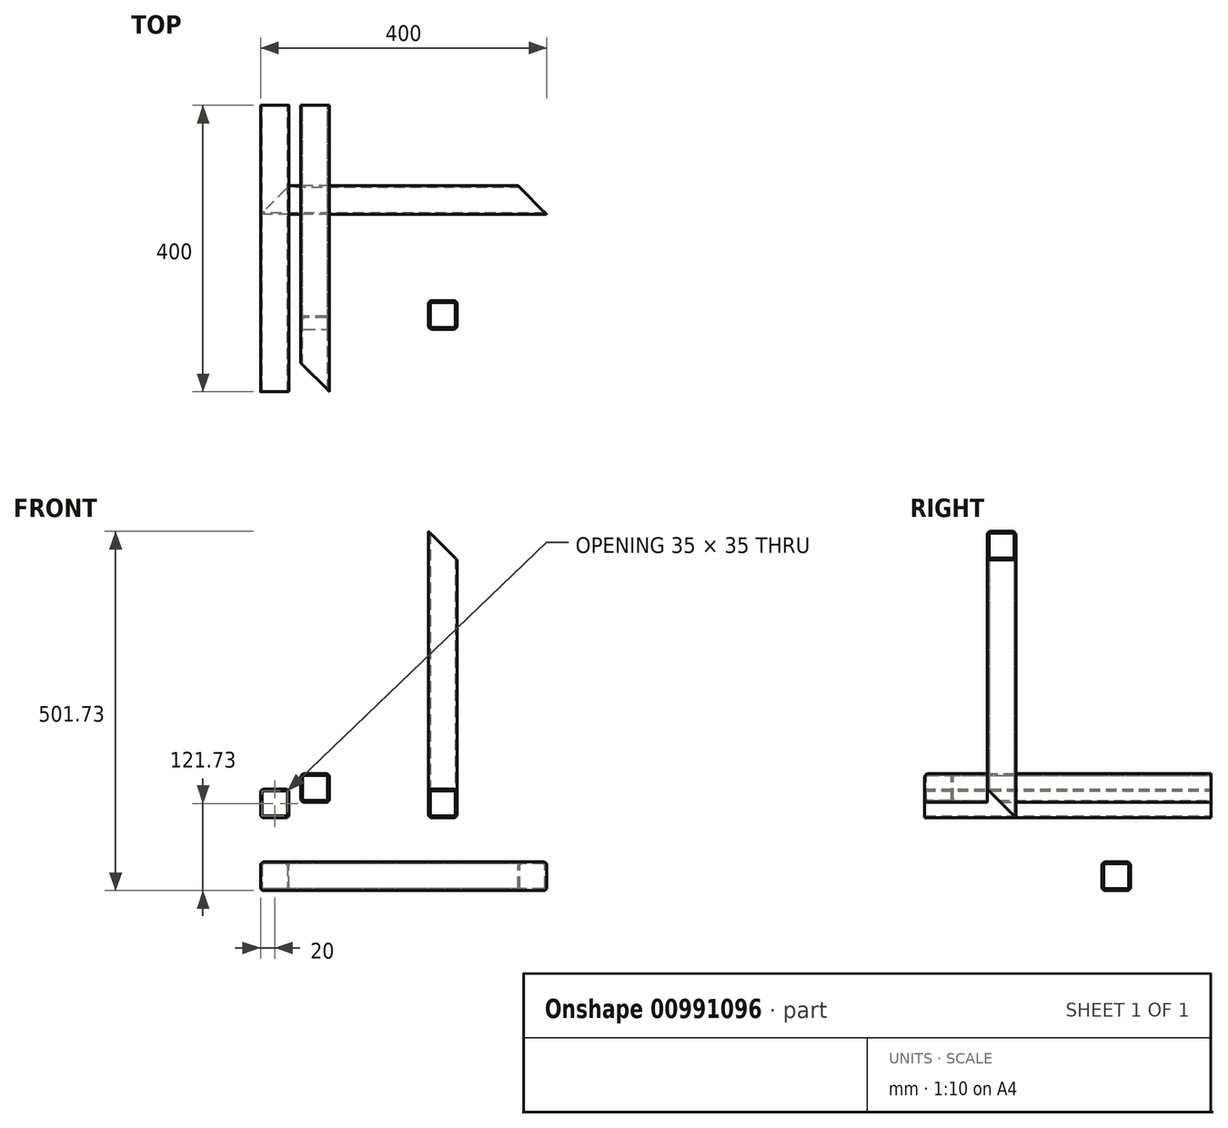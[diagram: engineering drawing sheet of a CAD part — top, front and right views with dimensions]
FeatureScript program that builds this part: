
annotation { "Feature Type Name" : "Feature", "Feature Type Description" : "" }
export const myFeature = defineFeature(function(context is Context, id is Id, definition is map)
    precondition{}
    {
        {
            var Q0;
            Q0=qCreatedBy(makeId("Front.planeOp"),FACE);
            var sketch = newSketch(context, id + "F0", { "sketchPlane" : qUnion([Q0])});
            skLineSegment(sketch, "E0.bottom", {"start": v(5, 0) * mm, "end": v(35, 0) * mm});
            skLineSegment(sketch, "E0.top", {"start": v(5, 40) * mm, "end": v(35, 40) * mm});
            skLineSegment(sketch, "E0.left", {"start": v(0, 5) * mm, "end": v(0, 35) * mm});
            skLineSegment(sketch, "E0.right", {"start": v(40, 5) * mm, "end": v(40, 35) * mm});
            skPoint(sketch, "E1.visualSharp", {"position": v(0, 40) * mm});
            skArc(sketch, "E1.filletArc", {"start": v(5, 40) * mm, "mid": v(1.46, 38.54) * mm, "end": v(0, 35) * mm});
            skPoint(sketch, "E2.visualSharp", {"position": v(40, 40) * mm});
            skArc(sketch, "E2.filletArc", {"start": v(40, 35) * mm, "mid": v(38.54, 38.54) * mm, "end": v(35, 40) * mm});
            skPoint(sketch, "E3.visualSharp", {"position": v(40, 0) * mm});
            skArc(sketch, "E3.filletArc", {"start": v(35, 0) * mm, "mid": v(38.54, 1.46) * mm, "end": v(40, 5) * mm});
            skPoint(sketch, "E4.visualSharp", {"position": v(0, 0) * mm});
            skArc(sketch, "E4.filletArc", {"start": v(0, 5) * mm, "mid": v(1.46, 1.46) * mm, "end": v(5, 0) * mm});
            skLineSegment(sketch, "E5.0", {"start": v(5, 2.5) * mm, "end": v(35, 2.5) * mm});
            skLineSegment(sketch, "E5.1", {"start": v(2.5, 5) * mm, "end": v(2.5, 35) * mm});
            skLineSegment(sketch, "E5.2", {"start": v(5, 37.5) * mm, "end": v(35, 37.5) * mm});
            skLineSegment(sketch, "E5.3", {"start": v(37.5, 5) * mm, "end": v(37.5, 35) * mm});
            skPoint(sketch, "E6.visualSharp", {"position": v(2.5, 2.5) * mm});
            skArc(sketch, "E6.filletArc", {"start": v(2.5, 5) * mm, "mid": v(3.23, 3.23) * mm, "end": v(5, 2.5) * mm});
            skPoint(sketch, "E7.visualSharp", {"position": v(2.5, 37.5) * mm});
            skArc(sketch, "E7.filletArc", {"start": v(5, 37.5) * mm, "mid": v(3.23, 36.77) * mm, "end": v(2.5, 35) * mm});
            skPoint(sketch, "E8.visualSharp", {"position": v(37.5, 37.5) * mm});
            skArc(sketch, "E8.filletArc", {"start": v(37.5, 35) * mm, "mid": v(36.77, 36.77) * mm, "end": v(35, 37.5) * mm});
            skPoint(sketch, "E9.visualSharp", {"position": v(37.5, 2.5) * mm});
            skArc(sketch, "E9.filletArc", {"start": v(35, 2.5) * mm, "mid": v(36.77, 3.23) * mm, "end": v(37.5, 5) * mm});
            skSolve(sketch);
        }
        {
            var Q0;
            Q0=makeQuery(id+"F0.imprint","IMPRINT",FACE,{"disambiguationData":[TD([[makeQuery(id+"F0.imprint","IMPRINT",EDGE,{"derivedFrom":sQuery(id+"F0.wireOp",EDGE,"E0.bottom")}),1.0]])]});
            extrude(context, id + "F1", {"entities" : qUnion([Q0]), "depth" : 400 * mm, "offsetDistance" : 25 * mm});
        }
        {
            var Q0;
            Q0=qCreatedBy(makeId("Right.planeOp"),FACE);
            var sketch = newSketch(context, id + "F2", { "sketchPlane" : qUnion([Q0])});
            skLineSegment(sketch, "E10.bottom", {"start": v(-147.53, -101.73) * mm, "end": v(-117.53, -101.73) * mm});
            skLineSegment(sketch, "E10.top", {"start": v(-147.53, -61.73) * mm, "end": v(-117.53, -61.73) * mm});
            skLineSegment(sketch, "E10.left", {"start": v(-152.53, -96.73) * mm, "end": v(-152.53, -66.73) * mm});
            skLineSegment(sketch, "E10.right", {"start": v(-112.53, -96.73) * mm, "end": v(-112.53, -66.73) * mm});
            skPoint(sketch, "E11.visualSharp", {"position": v(-152.53, -61.73) * mm});
            skArc(sketch, "E11.filletArc", {"start": v(-147.53, -61.73) * mm, "mid": v(-151.06, -63.2) * mm, "end": v(-152.53, -66.73) * mm});
            skPoint(sketch, "E12.visualSharp", {"position": v(-112.53, -61.73) * mm});
            skArc(sketch, "E12.filletArc", {"start": v(-112.53, -66.73) * mm, "mid": v(-114, -63.2) * mm, "end": v(-117.53, -61.73) * mm});
            skPoint(sketch, "E13.visualSharp", {"position": v(-112.53, -101.73) * mm});
            skArc(sketch, "E13.filletArc", {"start": v(-117.53, -101.73) * mm, "mid": v(-114, -100.26) * mm, "end": v(-112.53, -96.73) * mm});
            skPoint(sketch, "E14.visualSharp", {"position": v(-152.53, -101.73) * mm});
            skArc(sketch, "E14.filletArc", {"start": v(-152.53, -96.73) * mm, "mid": v(-151.06, -100.26) * mm, "end": v(-147.53, -101.73) * mm});
            skLineSegment(sketch, "E15.0", {"start": v(-147.53, -99.23) * mm, "end": v(-117.53, -99.23) * mm});
            skLineSegment(sketch, "E15.1", {"start": v(-150.03, -96.73) * mm, "end": v(-150.03, -66.73) * mm});
            skLineSegment(sketch, "E15.2", {"start": v(-147.53, -64.23) * mm, "end": v(-117.53, -64.23) * mm});
            skLineSegment(sketch, "E15.3", {"start": v(-115.03, -96.73) * mm, "end": v(-115.03, -66.73) * mm});
            skPoint(sketch, "E16.visualSharp", {"position": v(-150.03, -99.23) * mm});
            skArc(sketch, "E16.filletArc", {"start": v(-150.03, -96.73) * mm, "mid": v(-149.3, -98.5) * mm, "end": v(-147.53, -99.23) * mm});
            skPoint(sketch, "E17.visualSharp", {"position": v(-150.03, -64.23) * mm});
            skArc(sketch, "E17.filletArc", {"start": v(-147.53, -64.23) * mm, "mid": v(-149.3, -64.96) * mm, "end": v(-150.03, -66.73) * mm});
            skPoint(sketch, "E18.visualSharp", {"position": v(-115.03, -64.23) * mm});
            skArc(sketch, "E18.filletArc", {"start": v(-115.03, -66.73) * mm, "mid": v(-115.76, -64.96) * mm, "end": v(-117.53, -64.23) * mm});
            skPoint(sketch, "E19.visualSharp", {"position": v(-115.03, -99.23) * mm});
            skArc(sketch, "E19.filletArc", {"start": v(-117.53, -99.23) * mm, "mid": v(-115.76, -98.5) * mm, "end": v(-115.03, -96.73) * mm});
            skSolve(sketch);
        }
        {
            var Q0;
            Q0=makeQuery(id+"F2.imprint","IMPRINT",FACE,{"disambiguationData":[TD([[makeQuery(id+"F2.imprint","IMPRINT",EDGE,{"derivedFrom":sQuery(id+"F2.wireOp",EDGE,"E10.bottom")}),1.0]])]});
            extrude(context, id + "F3", {"entities" : qUnion([Q0]), "depth" : 400 * mm, "offsetDistance" : 25 * mm});
        }
        {
            var Q0;
            Q0=makeQuery(id+"F1.opExtrude","SWEPT_FACE",FACE,{"disambiguationData":[OSD([sQuery(id+"F0.wireOp",EDGE,"E0.top")])]});
            var sketch = newSketch(context, id + "F4", { "sketchPlane" : qUnion([Q0])});
            skLineSegment(sketch, "E20", {"start": v(40, -360) * mm, "end": v(40, -400) * mm});
            skLineSegment(sketch, "E21", {"start": v(40, -400) * mm, "end": v(0, -400) * mm});
            skLineSegment(sketch, "E22", {"start": v(0, -400) * mm, "end": v(40, -360) * mm});
            skSolve(sketch);
        }
        {
            var Q0;
            Q0 = qSketchRegion(id + "F4", true);
            extrude(context, id + "F5", {"entities" : qUnion([Q0]), "operationType" : NewBodyOperationType.REMOVE, "oppositeDirection" : true, "depth" : 40 * mm, "offsetDistance" : 25 * mm});
        }
        {
            var Q0;
            Q0=makeQuery(id+"F1.opExtrude","SWEPT_FACE",FACE,{"disambiguationData":[OSD([sQuery(id+"F0.wireOp",EDGE,"E0.right")])]});
            var sketch = newSketch(context, id + "F6", { "sketchPlane" : qUnion([Q0])});
            skLineSegment(sketch, "E23", {"start": v(-40, 40) * mm, "end": v(0, 40) * mm});
            skLineSegment(sketch, "E24", {"start": v(0, 40) * mm, "end": v(0, 0) * mm});
            skLineSegment(sketch, "E25", {"start": v(0, 0) * mm, "end": v(-40, 40) * mm});
            skSolve(sketch);
        }
        {
            var Q0;
            Q0 = qSketchRegion(id + "F6", true);
            extrude(context, id + "F7", {"entities" : qUnion([Q0]), "operationType" : NewBodyOperationType.REMOVE, "oppositeDirection" : true, "depth" : 40 * mm, "offsetDistance" : 25 * mm});
        }
        {
            var Q0;
            Q0=makeQuery(id+"F3.opExtrude","SWEPT_FACE",FACE,{"disambiguationData":[OSD([sQuery(id+"F2.wireOp",EDGE,"E10.top")])]});
            var sketch = newSketch(context, id + "F8", { "sketchPlane" : qUnion([Q0])});
            skLineSegment(sketch, "E26", {"start": v(0, -112.53) * mm, "end": v(40, -112.53) * mm});
            skLineSegment(sketch, "E27", {"start": v(40, -112.53) * mm, "end": v(0, -152.53) * mm});
            skLineSegment(sketch, "E28", {"start": v(0, -152.53) * mm, "end": v(0, -112.53) * mm});
            skLineSegment(sketch, "E29", {"start": v(360, -112.53) * mm, "end": v(400, -112.53) * mm});
            skLineSegment(sketch, "E30", {"start": v(400, -112.53) * mm, "end": v(400, -152.53) * mm});
            skLineSegment(sketch, "E31", {"start": v(400, -152.53) * mm, "end": v(360, -112.53) * mm});
            skSolve(sketch);
        }
        {
            var Q0;
            Q0 = qSketchRegion(id + "F8", true);
            extrude(context, id + "F9", {"entities" : qUnion([Q0]), "operationType" : NewBodyOperationType.REMOVE, "oppositeDirection" : true, "depth" : 40 * mm, "offsetDistance" : 25 * mm});
        }
        {
            var Q0;
            Q0=qCreatedBy(makeId("Front.planeOp"),FACE);
            var sketch = newSketch(context, id + "F10", { "sketchPlane" : qUnion([Q0])});
            skLineSegment(sketch, "E32.bottom", {"start": v(61.46, 21.54) * mm, "end": v(91.46, 21.54) * mm});
            skLineSegment(sketch, "E32.top", {"start": v(61.46, 61.54) * mm, "end": v(91.46, 61.54) * mm});
            skLineSegment(sketch, "E32.left", {"start": v(56.46, 26.54) * mm, "end": v(56.46, 56.54) * mm});
            skLineSegment(sketch, "E32.right", {"start": v(96.46, 26.54) * mm, "end": v(96.46, 56.54) * mm});
            skPoint(sketch, "E33.visualSharp", {"position": v(56.46, 61.54) * mm});
            skArc(sketch, "E33.filletArc", {"start": v(61.46, 61.54) * mm, "mid": v(57.92, 60.08) * mm, "end": v(56.46, 56.54) * mm});
            skPoint(sketch, "E34.visualSharp", {"position": v(96.46, 61.54) * mm});
            skArc(sketch, "E34.filletArc", {"start": v(96.46, 56.54) * mm, "mid": v(95, 60.08) * mm, "end": v(91.46, 61.54) * mm});
            skPoint(sketch, "E35.visualSharp", {"position": v(96.46, 21.54) * mm});
            skArc(sketch, "E35.filletArc", {"start": v(91.46, 21.54) * mm, "mid": v(95, 23) * mm, "end": v(96.46, 26.54) * mm});
            skPoint(sketch, "E36.visualSharp", {"position": v(56.46, 21.54) * mm});
            skArc(sketch, "E36.filletArc", {"start": v(56.46, 26.54) * mm, "mid": v(57.92, 23) * mm, "end": v(61.46, 21.54) * mm});
            skLineSegment(sketch, "E37.0", {"start": v(61.46, 24.04) * mm, "end": v(91.46, 24.04) * mm});
            skLineSegment(sketch, "E37.1", {"start": v(58.96, 26.54) * mm, "end": v(58.96, 56.54) * mm});
            skLineSegment(sketch, "E37.2", {"start": v(61.46, 59.04) * mm, "end": v(91.46, 59.04) * mm});
            skLineSegment(sketch, "E37.3", {"start": v(93.96, 26.54) * mm, "end": v(93.96, 56.54) * mm});
            skPoint(sketch, "E38.visualSharp", {"position": v(58.96, 24.04) * mm});
            skArc(sketch, "E38.filletArc", {"start": v(58.96, 26.54) * mm, "mid": v(59.7, 24.78) * mm, "end": v(61.46, 24.04) * mm});
            skPoint(sketch, "E39.visualSharp", {"position": v(58.96, 59.04) * mm});
            skArc(sketch, "E39.filletArc", {"start": v(61.46, 59.04) * mm, "mid": v(59.7, 58.31) * mm, "end": v(58.96, 56.54) * mm});
            skPoint(sketch, "E40.visualSharp", {"position": v(93.96, 59.04) * mm});
            skArc(sketch, "E40.filletArc", {"start": v(93.96, 56.54) * mm, "mid": v(93.23, 58.31) * mm, "end": v(91.46, 59.04) * mm});
            skPoint(sketch, "E41.visualSharp", {"position": v(93.96, 24.04) * mm});
            skArc(sketch, "E41.filletArc", {"start": v(91.46, 24.04) * mm, "mid": v(93.23, 24.78) * mm, "end": v(93.96, 26.54) * mm});
            skSolve(sketch);
        }
        {
            var Q0;
            Q0 = qSketchRegion(id + "F10", true);
            extrude(context, id + "F11", {"entities" : qUnion([Q0]), "depth" : 400 * mm, "offsetDistance" : 25 * mm});
        }
        {
            var Q0;
            Q0=makeQuery(id+"F11.opExtrude","SWEPT_FACE",FACE,{"disambiguationData":[OSD([sQuery(id+"F10.wireOp",EDGE,"E32.top")])]});
            var sketch = newSketch(context, id + "F12", { "sketchPlane" : qUnion([Q0])});
            skLineSegment(sketch, "E42", {"start": v(56.46, -400) * mm, "end": v(56.46, -360) * mm});
            skLineSegment(sketch, "E43", {"start": v(56.46, -360) * mm, "end": v(96.46, -400) * mm});
            skLineSegment(sketch, "E44", {"start": v(96.46, -400) * mm, "end": v(56.46, -400) * mm});
            skSolve(sketch);
        }
        {
            var Q0;
            Q0 = qSketchRegion(id + "F12", true);
            extrude(context, id + "F13", {"entities" : qUnion([Q0]), "operationType" : NewBodyOperationType.REMOVE, "endBound" : BoundingType.THROUGH_ALL, "oppositeDirection" : true, "depth" : 25 * mm, "offsetDistance" : 25 * mm});
        }
        {
            var Q0;
            Q0=qCreatedBy(makeId("Top.planeOp"),FACE);
            var sketch = newSketch(context, id + "F14", { "sketchPlane" : qUnion([Q0])});
            skLineSegment(sketch, "E45.bottom", {"start": v(239.63, -312.64) * mm, "end": v(269.63, -312.64) * mm});
            skLineSegment(sketch, "E45.top", {"start": v(239.63, -272.64) * mm, "end": v(269.63, -272.64) * mm});
            skLineSegment(sketch, "E45.left", {"start": v(234.63, -307.64) * mm, "end": v(234.63, -277.64) * mm});
            skLineSegment(sketch, "E45.right", {"start": v(274.63, -307.64) * mm, "end": v(274.63, -277.64) * mm});
            skPoint(sketch, "E46.visualSharp", {"position": v(234.63, -272.64) * mm});
            skArc(sketch, "E46.filletArc", {"start": v(239.63, -272.64) * mm, "mid": v(236.1, -274.1) * mm, "end": v(234.63, -277.64) * mm});
            skPoint(sketch, "E47.visualSharp", {"position": v(274.63, -272.64) * mm});
            skArc(sketch, "E47.filletArc", {"start": v(274.63, -277.64) * mm, "mid": v(273.17, -274.1) * mm, "end": v(269.63, -272.64) * mm});
            skPoint(sketch, "E48.visualSharp", {"position": v(274.63, -312.64) * mm});
            skArc(sketch, "E48.filletArc", {"start": v(269.63, -312.64) * mm, "mid": v(273.17, -311.18) * mm, "end": v(274.63, -307.64) * mm});
            skPoint(sketch, "E49.visualSharp", {"position": v(234.63, -312.64) * mm});
            skArc(sketch, "E49.filletArc", {"start": v(234.63, -307.64) * mm, "mid": v(236.1, -311.18) * mm, "end": v(239.63, -312.64) * mm});
            skLineSegment(sketch, "E50.0", {"start": v(239.63, -310.14) * mm, "end": v(269.63, -310.14) * mm});
            skLineSegment(sketch, "E50.1", {"start": v(237.13, -307.64) * mm, "end": v(237.13, -277.64) * mm});
            skLineSegment(sketch, "E50.2", {"start": v(239.63, -275.14) * mm, "end": v(269.63, -275.14) * mm});
            skLineSegment(sketch, "E50.3", {"start": v(272.13, -307.64) * mm, "end": v(272.13, -277.64) * mm});
            skPoint(sketch, "E51.visualSharp", {"position": v(237.13, -310.14) * mm});
            skArc(sketch, "E51.filletArc", {"start": v(237.13, -307.64) * mm, "mid": v(237.86, -309.41) * mm, "end": v(239.63, -310.14) * mm});
            skPoint(sketch, "E52.visualSharp", {"position": v(237.13, -275.14) * mm});
            skArc(sketch, "E52.filletArc", {"start": v(239.63, -275.14) * mm, "mid": v(237.86, -275.88) * mm, "end": v(237.13, -277.64) * mm});
            skPoint(sketch, "E53.visualSharp", {"position": v(272.13, -275.14) * mm});
            skArc(sketch, "E53.filletArc", {"start": v(272.13, -277.64) * mm, "mid": v(271.4, -275.88) * mm, "end": v(269.63, -275.14) * mm});
            skPoint(sketch, "E54.visualSharp", {"position": v(272.13, -310.14) * mm});
            skArc(sketch, "E54.filletArc", {"start": v(269.63, -310.14) * mm, "mid": v(271.4, -309.41) * mm, "end": v(272.13, -307.64) * mm});
            skSolve(sketch);
        }
        {
            var Q0;
            Q0 = qSketchRegion(id + "F14", true);
            extrude(context, id + "F15", {"entities" : qUnion([Q0]), "depth" : 400 * mm, "offsetDistance" : 25 * mm});
        }
        {
            var Q0;
            Q0=makeQuery(id+"F15.opExtrude","SWEPT_FACE",FACE,{"disambiguationData":[OSD([sQuery(id+"F14.wireOp",EDGE,"E45.right")])]});
            var sketch = newSketch(context, id + "F16", { "sketchPlane" : qUnion([Q0])});
            skLineSegment(sketch, "E55", {"start": v(-312.64, 0) * mm, "end": v(-272.64, 0) * mm});
            skLineSegment(sketch, "E56", {"start": v(-272.64, 0) * mm, "end": v(-312.64, 40) * mm});
            skLineSegment(sketch, "E57", {"start": v(-312.64, 40) * mm, "end": v(-312.64, 0) * mm});
            skSolve(sketch);
        }
        {
            var Q0;
            Q0 = qSketchRegion(id + "F16", true);
            extrude(context, id + "F17", {"entities" : qUnion([Q0]), "operationType" : NewBodyOperationType.REMOVE, "endBound" : BoundingType.THROUGH_ALL, "oppositeDirection" : true, "depth" : 25 * mm, "offsetDistance" : 25 * mm});
        }
        {
            var Q0;
            Q0=makeQuery(id+"F15.opExtrude","SWEPT_FACE",FACE,{"disambiguationData":[OSD([sQuery(id+"F14.wireOp",EDGE,"E45.bottom")])]});
            var sketch = newSketch(context, id + "F18", { "sketchPlane" : qUnion([Q0])});
            skLineSegment(sketch, "E58", {"start": v(234.63, 400) * mm, "end": v(274.63, 400) * mm});
            skLineSegment(sketch, "E59", {"start": v(274.63, 400) * mm, "end": v(274.63, 360) * mm});
            skLineSegment(sketch, "E60", {"start": v(274.63, 360) * mm, "end": v(234.63, 400) * mm});
            skSolve(sketch);
        }
        {
            var Q0;
            Q0 = qSketchRegion(id + "F18", true);
            extrude(context, id + "F19", {"entities" : qUnion([Q0]), "operationType" : NewBodyOperationType.REMOVE, "endBound" : BoundingType.THROUGH_ALL, "oppositeDirection" : true, "depth" : 25 * mm, "offsetDistance" : 25 * mm});
        }
        {
            var Q0;
            Q0 = qSketchRegion(id + "F0", true);
            extrude(context, id + "F20", {"entities" : qUnion([Q0]), "operationType" : NewBodyOperationType.ADD, "depth" : 400 * mm, "offsetDistance" : 25 * mm});
        }
    });
